# Revit family: X7011
name_source: partatom
category: Mechanical Equipment
revit_build: Autodesk Revit 2013 (Build: 20120221_2030(x64)
units: mm (PartAtom-declared; Revit-internal decimal feet)

## types (6) — shared parameters
Assembly Code = D2010900
Configuration = Reversing
Cutter & Plate = SS Hardened to 55-60 Rockwell
Default Elevation = 0"
Description = Commercial Effluent Pumps
Discharge Diameter = 1.25" NPT
Discharge Height = 5 3/8"
Discharge Radius = 5/8"
Flow @ 5' = 38 GPM
Hertz = 60
Impeller Diameter = 5 17/32"
Impeller Trim - Reversing Models Only (Optional) = Yes
Impeller Type = Vortex
Installation Type = Floor Mounted
Insulation = Class F
Lead Wires Insulation = Class F
Length = 11 27/32"
Manufacturer = Zoeller
Masterformat Number = 33 36 16
Masterformat Title = Utility Septic Tank Effluent Pumps
Material = Cast Iron-Zoeller-Powder Coated Epoxy
Max. Stator Temp. = 311 °F
Max. Water Temp. = 104 °F
Maximum KW Input = 3.9
Model = X7011
Moisture Sensor (Optional) = Moisture Sensing Probes (Requires a circuit in control panel)
Motor = 2.0 Pump Name Plate Horsepower
Motor Shaft = 416 S.S.
Motor Thermal Shutoff = Therman Sensors
Motor Type = Submersible Explosion Proof
NEC Locked Rotor Code = K
O-Rings = Viton
Omniclass Table 23 Code = 23.60.30.21
Omniclass Table 23 Title = Pumps
Operation = Non-Automatic
Overall Height = 26 31/32"
Power Cord = 14 Gauge SOW
Price = Prices may vary. Please consult Manufacturer Representative for most up-to-date price list.
Product Page URL = http://www.zoellerengprod.com
RPM = 3450
Service Factor = 1.2
Shaft Seal Lower (Options) = Silicon Carbide/Silicon Carbide
Shaft Seal Lower Standard = Carbon/Silicon Carbide
Shaft Seal Upper (Options) = Carbon/Silicon Carbide, Silicon Carbide/Silicon Carbide
Shaft Seal Upper Standard = Carbon/Ceramic
Tandem Seals = Standard
Type SOW Power Cord Length = 240"
URL = http://www.zoellerengprod.com
Warranty Information = 36 Months (Limited)
Waste Connection = Yes
Width = 8 1/2"

## per-type parameters (varying)
| type | Apparent Load | Full Load Amps (Voltage Dependent) | Locked Rotor Amps | Motor Design Letter | Phase | Shipping Weight | Type | Voltage |
| X7011 - 200V 1Ph | 4000 VA | 20.0 | 60.7 | NEMA L | 1 | 139 lbs. | Split Capacitor | 200 V |
| X7011 - 230V 1Ph | 3956 VA | 17.2 | 57.3 | NEMA L | 1 | 139 lbs. | Split Capacitor | 230 V |
| X7011 - 200V 3Ph | 2460 VA | 12.3 | 47.0 | NEMA B | 3 | 132 lbs. | 3 Phase | 200 V |
| X7011 - 230V 3Ph | 2484 VA | 10.8 | 41.9 | NEMA B | 3 | 132 lbs. | 3 Phase | 230 V |
| X7011 - 460V 3Ph | 2530 VA | 5.5 | 20.6 | NEMA B | 3 | 132 lbs. | 3 Phase | 460 V |
| X7011 - 575V 3Ph | 2588 VA | 4.5 | 16.2 | NEMA B | 3 | 132 lbs. | 3 Phase | 575 V |

## geometry (parser evidence)
native form markers: Blend x6
no freeform markers — native parametric forms only
